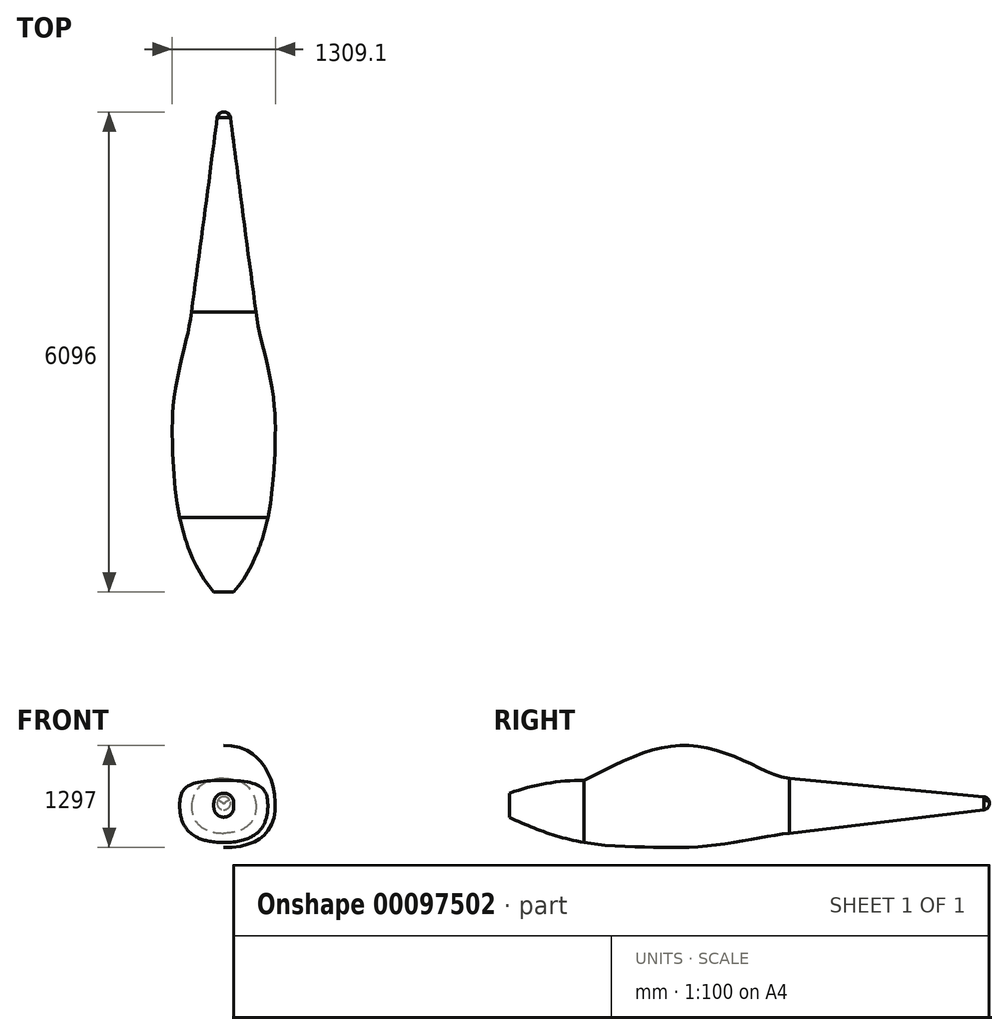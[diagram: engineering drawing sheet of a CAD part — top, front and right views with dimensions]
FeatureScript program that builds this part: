
annotation { "Feature Type Name" : "Feature", "Feature Type Description" : "" }
export const myFeature = defineFeature(function(context is Context, id is Id, definition is map)
    precondition{}
    {
        {
            var Q0;
            Q0=qCreatedBy(makeId("Right.planeOp"),FACE);
            var sketch = newSketch(context, id + "F0", { "sketchPlane" : qUnion([Q0])});
            skPoint(sketch, "E0", {"position": v(6096, 0) * mm});
            skLineSegment(sketch, "E1", {"start": v(0, 127) * mm, "end": v(0, -177.8) * mm, "construction": true});
            skLineSegment(sketch, "E2", {"start": v(3556, 317.5) * mm, "end": v(6096, 76.2) * mm});
            skLineSegment(sketch, "E3", {"start": v(3556, -381) * mm, "end": v(6096, -76.2) * mm});
            skLineSegment(sketch, "E4", {"start": v(6096, 76.2) * mm, "end": v(6096, -76.2) * mm});
            skFitSpline(sketch, "E5", {"points": [v(3556, 317.5) * mm, v(3071.36, 497.5) * mm, v(2421.88, 718.32) * mm, v(1768.58, 660.46) * mm, v(947.27, 290.82) * mm], "startDerivative": vector(-2336.2, 221.94) * mm, "endDerivative": vector(-2919.53, -1478.23) * mm});
            skArc(sketch, "E6", {"start": v(947.27, 290.82) * mm, "mid": v(466.6, 249.56) * mm, "end": v(0, 127) * mm});
            skLineSegment(sketch, "E7", {"start": v(947.27, 290.82) * mm, "end": v(1552.32, 290.82) * mm, "construction": true});
            skLineSegment(sketch, "E8", {"start": v(3556, 317.5) * mm, "end": v(3556, -381) * mm, "construction": true});
            skLineSegment(sketch, "E9", {"start": v(0, 0) * mm, "end": v(6096, 0) * mm, "construction": true});
            skFitSpline(sketch, "E10", {"points": [v(0, -177.8) * mm, v(947.27, -499.76) * mm, v(1768.58, -558.74) * mm, v(2421.88, -551.68) * mm, v(3071.36, -461.35) * mm, v(3556, -381) * mm], "startDerivative": vector(4121.91, -2025.5) * mm, "endDerivative": vector(3446.33, 413.56) * mm});
            skLineSegment(sketch, "E11", {"start": v(947.27, 290.82) * mm, "end": v(947.27, -499.76) * mm, "construction": true});
            skSolve(sketch);
        }
        {
            var Q0;
            Q0=qCreatedBy(makeId("Top.planeOp"),FACE);
            var sketch = newSketch(context, id + "F1", { "sketchPlane" : qUnion([Q0])});
            skPoint(sketch, "E12", {"position": v(0, 0) * mm});
            skPoint(sketch, "E13", {"position": v(0, 4938.15) * mm});
            skLineSegment(sketch, "E14", {"start": v(0, -719) * mm, "end": v(0, 5523.82) * mm, "construction": true});
            skLineSegment(sketch, "E15", {"start": v(-6987.12, -719) * mm, "end": v(5143.5, 8679) * mm, "construction": true});
            skLineSegment(sketch, "E16", {"start": v(0, 0) * mm, "end": v(127, 0) * mm, "construction": true});
            skPoint(sketch, "E17", {"position": v(0, 3556) * mm});
            skLineSegment(sketch, "E18", {"start": v(0, 3556) * mm, "end": v(406.4, 3556) * mm, "construction": true});
            skLineSegment(sketch, "E19", {"start": v(0, 6096) * mm, "end": v(76.2, 6096) * mm, "construction": true});
            skLineSegment(sketch, "E20", {"start": v(76.2, 6096) * mm, "end": v(406.4, 3556) * mm});
            skFitSpline(sketch, "E21", {"points": [v(406.4, 3556) * mm, v(508, 3071.36) * mm, v(635, 2421.88) * mm, v(647.7, 1768.58) * mm, v(558.8, 947.27) * mm, v(127, 0) * mm], "startDerivative": vector(419.27, -3225.13) * mm, "endDerivative": vector(-3018.7, -3495.33) * mm, "construction": true});
            skFitSpline(sketch, "E22", {"points": [v(558.8, 947.27) * mm, v(647.7, 1768.58) * mm, v(635, 2421.88) * mm, v(508, 3071.36) * mm, v(406.4, 3556) * mm], "startDerivative": vector(669, 3233.18) * mm, "endDerivative": vector(-318.72, 2451.72) * mm});
            skSolve(sketch);
        }
        {
            var Q0;
            Q0=qCreatedBy(makeId("Front.planeOp"),FACE);
            var sketch = newSketch(context, id + "F2", { "sketchPlane" : qUnion([Q0])});
            skArc(sketch, "E23", {"start": v(127, 0) * mm, "mid": v(89.8, 89.8) * mm, "end": v(0, 127) * mm});
            skArc(sketch, "E24", {"start": v(0, -177.8) * mm, "mid": v(89.8, -140.6) * mm, "end": v(127, -50.8) * mm});
            skLineSegment(sketch, "E25", {"start": v(127, 0) * mm, "end": v(127, -50.8) * mm});
            skLineSegment(sketch, "E26", {"start": v(0, 127) * mm, "end": v(0, -177.8) * mm});
            skLineSegment(sketch, "E27", {"start": v(0, -177.8) * mm, "end": v(-68.56, -177.8) * mm, "construction": true});
            skSolve(sketch);
        }
        {
            var Q0;
            Q0=sQuery(id+"F0.wireOp",VERTEX,"E6.start");
            var Q1;
            Q1=sQuery(id+"F1.wireOp",VERTEX,"E21.4.internal");
            var Q2;
            Q2=sQuery(id+"F0.wireOp",VERTEX,"E10.1.internal");
            cPlane(context, id + "F3", {"entities" : qUnion([Q0, Q1, Q2]), "cplaneType" : CPlaneType.THREE_POINT, "offset" : 152.4 * mm, "width" : 152.4 * mm, "height" : 152.4 * mm});
        }
        {
            var Q0;
            Q0=qCreatedBy(id+"F3.planeOp",FACE);
            var sketch = newSketch(context, id + "F4", { "sketchPlane" : qUnion([Q0])});
            skLineSegment(sketch, "E28", {"start": v(0, 290.82) * mm, "end": v(-303.5, 290.82) * mm, "construction": true});
            skLineSegment(sketch, "E29", {"start": v(0, -499.76) * mm, "end": v(-303.5, -499.76) * mm, "construction": true});
            skLineSegment(sketch, "E30", {"start": v(0, 290.82) * mm, "end": v(0, -499.76) * mm});
            skFitSpline(sketch, "E31", {"points": [v(0, 290.82) * mm, v(558.8, 0) * mm, v(0, -499.76) * mm], "startDerivative": vector(3027.2, 0) * mm, "endDerivative": vector(-2921, 0) * mm});
            skSolve(sketch);
        }
        {
            var Q0;
            Q0=sQuery(id+"F0.wireOp",VERTEX,"E5.3.internal");
            var Q1;
            Q1=sQuery(id+"F1.wireOp",VERTEX,"E21.3.internal");
            var Q2;
            Q2=sQuery(id+"F0.wireOp",VERTEX,"E10.2.internal");
            cPlane(context, id + "F5", {"entities" : qUnion([Q0, Q1, Q2]), "cplaneType" : CPlaneType.THREE_POINT, "offset" : 152.4 * mm, "width" : 152.4 * mm, "height" : 152.4 * mm});
        }
        {
            var Q0;
            Q0=qCreatedBy(id+"F5.planeOp",FACE);
            var sketch = newSketch(context, id + "F6", { "sketchPlane" : qUnion([Q0])});
            skLineSegment(sketch, "E32", {"start": v(0, 660.46) * mm, "end": v(0, -558.74) * mm});
            skLineSegment(sketch, "E33", {"start": v(0, -558.74) * mm, "end": v(-265.3, -558.74) * mm, "construction": true});
            skLineSegment(sketch, "E34", {"start": v(0, 660.46) * mm, "end": v(-265.3, 660.46) * mm, "construction": true});
            skFitSpline(sketch, "E35", {"points": [v(0, 660.46) * mm, v(647.7, 0) * mm, v(0, -558.74) * mm], "startDerivative": vector(2690.55, 0) * mm, "endDerivative": vector(-3108.83, 0) * mm});
            skSolve(sketch);
        }
        {
            var Q0;
            Q0=sQuery(id+"F0.wireOp",VERTEX,"E5.2.internal");
            var Q1;
            Q1=sQuery(id+"F1.wireOp",VERTEX,"E21.2.internal");
            var Q2;
            Q2=sQuery(id+"F0.wireOp",VERTEX,"E10.3.internal");
            cPlane(context, id + "F7", {"entities" : qUnion([Q0, Q1, Q2]), "cplaneType" : CPlaneType.THREE_POINT, "offset" : 152.4 * mm, "width" : 152.4 * mm, "height" : 152.4 * mm});
        }
        {
            var Q0;
            Q0=qCreatedBy(id+"F7.planeOp",FACE);
            var sketch = newSketch(context, id + "F8", { "sketchPlane" : qUnion([Q0])});
            skLineSegment(sketch, "E36", {"start": v(-313.1, 718.32) * mm, "end": v(0, 718.32) * mm, "construction": true});
            skLineSegment(sketch, "E37", {"start": v(0, 718.32) * mm, "end": v(0, -551.68) * mm});
            skLineSegment(sketch, "E38", {"start": v(0, -551.68) * mm, "end": v(-313.1, -551.68) * mm, "construction": true});
            skFitSpline(sketch, "E39", {"points": [v(0, 718.32) * mm, v(635, 0) * mm, v(0, -551.68) * mm], "startDerivative": vector(2656.34, 0) * mm, "endDerivative": vector(-3151.03, 0) * mm});
            skSolve(sketch);
        }
        {
            var Q0;
            Q0=sQuery(id+"F0.wireOp",VERTEX,"E5.1.internal");
            var Q1;
            Q1=sQuery(id+"F1.wireOp",VERTEX,"E21.1.internal");
            var Q2;
            Q2=sQuery(id+"F0.wireOp",VERTEX,"E10.4.internal");
            cPlane(context, id + "F9", {"entities" : qUnion([Q0, Q1, Q2]), "cplaneType" : CPlaneType.THREE_POINT, "offset" : 152.4 * mm, "width" : 152.4 * mm, "height" : 152.4 * mm});
        }
        {
            var Q0;
            Q0=qCreatedBy(id+"F9.planeOp",FACE);
            var sketch = newSketch(context, id + "F10", { "sketchPlane" : qUnion([Q0])});
            skLineSegment(sketch, "E40", {"start": v(-243.65, 497.5) * mm, "end": v(0, 497.5) * mm, "construction": true});
            skLineSegment(sketch, "E41", {"start": v(0, 497.5) * mm, "end": v(0, -461.35) * mm});
            skLineSegment(sketch, "E42", {"start": v(0, -461.35) * mm, "end": v(-243.65, -461.35) * mm, "construction": true});
            skFitSpline(sketch, "E43", {"points": [v(0, 497.5) * mm, v(508, 0) * mm, v(0, -461.35) * mm], "startDerivative": vector(2265.88, 0) * mm, "endDerivative": vector(-2614.01, 0) * mm});
            skSolve(sketch);
        }
        {
            var Q0;
            Q0=sQuery(id+"F0.wireOp",VERTEX,"E2.start");
            var Q1;
            Q1=sQuery(id+"F1.wireOp",VERTEX,"E20.end");
            var Q2;
            Q2=sQuery(id+"F0.wireOp",VERTEX,"E8.end");
            cPlane(context, id + "F11", {"entities" : qUnion([Q0, Q1, Q2]), "cplaneType" : CPlaneType.THREE_POINT, "offset" : 152.4 * mm, "width" : 152.4 * mm, "height" : 152.4 * mm});
        }
        {
            var Q0;
            Q0=qCreatedBy(id+"F11.planeOp",FACE);
            var sketch = newSketch(context, id + "F12", { "sketchPlane" : qUnion([Q0])});
            skLineSegment(sketch, "E44", {"start": v(-254, 317.5) * mm, "end": v(0, 317.5) * mm, "construction": true});
            skLineSegment(sketch, "E45", {"start": v(0, 317.5) * mm, "end": v(0, -381) * mm});
            skLineSegment(sketch, "E46", {"start": v(0, -381) * mm, "end": v(-254, -381) * mm, "construction": true});
            skFitSpline(sketch, "E47", {"points": [v(0, 317.5) * mm, v(406.4, 0) * mm, v(0, -381) * mm], "startDerivative": vector(1553.96, 0) * mm, "endDerivative": vector(-1943.73, 0) * mm});
            skSolve(sketch);
        }
        {
            var Q0;
            Q0=sQuery(id+"F0.wireOp",VERTEX,"E2.end");
            var Q1;
            Q1=sQuery(id+"F1.wireOp",VERTEX,"E19.end");
            var Q2;
            Q2=sQuery(id+"F0.wireOp",VERTEX,"E4.end");
            cPlane(context, id + "F13", {"entities" : qUnion([Q0, Q1, Q2]), "cplaneType" : CPlaneType.THREE_POINT, "offset" : 152.4 * mm, "width" : 152.4 * mm, "height" : 152.4 * mm});
        }
        {
            var Q0;
            Q0=qCreatedBy(id+"F13.planeOp",FACE);
            var sketch = newSketch(context, id + "F14", { "sketchPlane" : qUnion([Q0])});
            skArc(sketch, "E48", {"start": v(0, -76.2) * mm, "mid": v(76.2, 0) * mm, "end": v(0, 76.2) * mm});
            skLineSegment(sketch, "E49", {"start": v(0, 76.2) * mm, "end": v(0, -76.2) * mm});
            skSolve(sketch);
        }
        {
            var Q0;
            Q0=qCreatedBy(makeId("Right.planeOp"),FACE);
            var sketch = newSketch(context, id + "F15", { "sketchPlane" : qUnion([Q0])});
            skFitSpline(sketch, "E50", {"points": [v(0, -177.8) * mm, v(947.27, -499.76) * mm], "startDerivative": vector(903.58, -444.02) * mm, "endDerivative": vector(1097.35, -206.55) * mm});
            skSolve(sketch);
        }
        {
            var Q0;
            Q0=qCreatedBy(makeId("Top.planeOp"),FACE);
            var sketch = newSketch(context, id + "F16", { "sketchPlane" : qUnion([Q0])});
            skFitSpline(sketch, "E51", {"points": [v(127, 0) * mm, v(438.27, 531.01) * mm, v(558.8, 947.27) * mm], "startDerivative": vector(781.47, 904.86) * mm, "endDerivative": vector(204.1, 910.7) * mm});
            skSolve(sketch);
        }
        {
            var Q0;
            Q0=makeQuery(id+"F2.imprint","IMPRINT",FACE,{"disambiguationData":[TD([[makeQuery(id+"F2.imprint","IMPRINT",EDGE,{"derivedFrom":sQuery(id+"F2.wireOp",EDGE,"E23")}),1.0]])]});
            var Q1;
            Q1=makeQuery(id+"F4.imprint","IMPRINT",FACE,{"disambiguationData":[TD([[makeQuery(id+"F4.imprint","IMPRINT",EDGE,{"derivedFrom":sQuery(id+"F4.wireOp",EDGE,"E30")}),1.0]])]});
            var Q2;
            Q2=sQuery(id+"F0.wireOp",EDGE,"E6");
            var Q3;
            Q3=sQuery(id+"F15.wireOp",EDGE,"E50");
            var Q4;
            Q4=sQuery(id+"F16.wireOp",EDGE,"E51");
            loft(context, id + "F17", {"addGuides" : true, "sheetProfilesArray" : [{ "sheetProfileEntities" : qUnion([Q0]) }, { "sheetProfileEntities" : qUnion([Q1]) }], "guidesArray" : [{ "guideEntities" : qUnion([Q2]), "guideDerivativeType" : LoftGuideDerivativeType.DEFAULT, "guideDerivativeMagnitude" : 1 }, { "guideEntities" : qUnion([Q3]), "guideDerivativeType" : LoftGuideDerivativeType.DEFAULT, "guideDerivativeMagnitude" : 1 }, { "guideEntities" : qUnion([Q4]), "guideDerivativeType" : LoftGuideDerivativeType.DEFAULT, "guideDerivativeMagnitude" : 1 }]});
        }
        {
            var Q0;
            Q0=qCreatedBy(makeId("Right.planeOp"),FACE);
            var sketch = newSketch(context, id + "F18", { "sketchPlane" : qUnion([Q0])});
            skFitSpline(sketch, "E52", {"points": [v(947.27, -499.76) * mm, v(1768.58, -558.74) * mm, v(2421.88, -551.68) * mm, v(3071.36, -461.35) * mm, v(3556, -381) * mm], "startDerivative": vector(3130, -509) * mm, "endDerivative": vector(2033.65, 244.04) * mm});
            skSolve(sketch);
        }
        {
            var Q1;
            Q1=makeQuery(id+"F17.opLoft","CAP_FACE",FACE,{"disambiguationData":[OSD([makeQuery(id+"F4.imprint","IMPRINT",FACE,{"disambiguationData":[TD([[makeQuery(id+"F4.imprint","IMPRINT",EDGE,{"derivedFrom":sQuery(id+"F4.wireOp",EDGE,"E30")}),1.0]])]})])],"isStart":true});
            var Q2;
            Q2=makeQuery(id+"F6.imprint","IMPRINT",FACE,{"disambiguationData":[TD([[makeQuery(id+"F6.imprint","IMPRINT",EDGE,{"derivedFrom":sQuery(id+"F6.wireOp",EDGE,"E32")}),1.0]])]});
            var Q3;
            Q3=makeQuery(id+"F8.imprint","IMPRINT",FACE,{"disambiguationData":[TD([[makeQuery(id+"F8.imprint","IMPRINT",EDGE,{"derivedFrom":sQuery(id+"F8.wireOp",EDGE,"E37")}),1.0]])]});
            var Q4;
            Q4=makeQuery(id+"F10.imprint","IMPRINT",FACE,{"disambiguationData":[TD([[makeQuery(id+"F10.imprint","IMPRINT",EDGE,{"derivedFrom":sQuery(id+"F10.wireOp",EDGE,"E41")}),1.0]])]});
            var Q5;
            Q5=makeQuery(id+"F12.imprint","IMPRINT",FACE,{"disambiguationData":[TD([[makeQuery(id+"F12.imprint","IMPRINT",EDGE,{"derivedFrom":sQuery(id+"F12.wireOp",EDGE,"E45")}),1.0]])]});
            var Q6;
            Q6=sQuery(id+"F1.wireOp",EDGE,"E22");
            var Q7;
            Q7=sQuery(id+"F0.wireOp",EDGE,"E5");
            var Q8;
            Q8=sQuery(id+"F18.wireOp",EDGE,"E52");
            loft(context, id + "F19", {"operationType" : NewBodyOperationType.ADD, "addGuides" : true, "sheetProfilesArray" : [{ "sheetProfileEntities" : qUnion([Q1]) }, { "sheetProfileEntities" : qUnion([Q2]) }, { "sheetProfileEntities" : qUnion([Q3]) }, { "sheetProfileEntities" : qUnion([Q4]) }, { "sheetProfileEntities" : qUnion([Q5]) }], "guidesArray" : [{ "guideEntities" : qUnion([Q6]), "guideDerivativeType" : LoftGuideDerivativeType.DEFAULT, "guideDerivativeMagnitude" : 1 }, { "guideEntities" : qUnion([Q7]), "guideDerivativeType" : LoftGuideDerivativeType.DEFAULT, "guideDerivativeMagnitude" : 1 }, { "guideEntities" : qUnion([Q8]), "guideDerivativeType" : LoftGuideDerivativeType.DEFAULT, "guideDerivativeMagnitude" : 1 }]});
        }
        {
            var Q1;
            Q1=makeQuery(id+"F19.opLoft","CAP_FACE",FACE,{"disambiguationData":[OSD([makeQuery(id+"F12.imprint","IMPRINT",FACE,{"disambiguationData":[TD([[makeQuery(id+"F12.imprint","IMPRINT",EDGE,{"derivedFrom":sQuery(id+"F12.wireOp",EDGE,"E45")}),1.0]])]})])],"isStart":true});
            var Q2;
            Q2=makeQuery(id+"F14.imprint","IMPRINT",FACE,{"disambiguationData":[TD([[makeQuery(id+"F14.imprint","IMPRINT",EDGE,{"derivedFrom":sQuery(id+"F14.wireOp",EDGE,"E48")}),1.0]])]});
            var Q3;
            Q3=sQuery(id+"F0.wireOp",EDGE,"E2");
            var Q4;
            Q4=sQuery(id+"F0.wireOp",EDGE,"E3");
            loft(context, id + "F20", {"operationType" : NewBodyOperationType.ADD, "addGuides" : true, "sheetProfilesArray" : [{ "sheetProfileEntities" : qUnion([Q1]) }, { "sheetProfileEntities" : qUnion([Q2]) }], "guidesArray" : [{ "guideEntities" : qUnion([Q3]), "guideDerivativeType" : LoftGuideDerivativeType.DEFAULT, "guideDerivativeMagnitude" : 1 }, { "guideEntities" : qUnion([Q4]), "guideDerivativeType" : LoftGuideDerivativeType.DEFAULT, "guideDerivativeMagnitude" : 1 }]});
        }
        {
            var Q0;
            Q0=makeQuery(id+"F17.opLoft","SWEPT_BODY",BODY,{"disambiguationData":[OSD([sQuery(id+"F0.wireOp",EDGE,"E6"),makeQuery(id+"F2.imprint","IMPRINT",FACE,{"disambiguationData":[TD([[makeQuery(id+"F2.imprint","IMPRINT",EDGE,{"derivedFrom":sQuery(id+"F2.wireOp",EDGE,"E23")}),1.0]])]}),makeQuery(id+"F4.imprint","IMPRINT",FACE,{"disambiguationData":[TD([[makeQuery(id+"F4.imprint","IMPRINT",EDGE,{"derivedFrom":sQuery(id+"F4.wireOp",EDGE,"E30")}),1.0]])]}),sQuery(id+"F15.wireOp",EDGE,"E50"),sQuery(id+"F16.wireOp",EDGE,"E51")])]});
            var Q1;
            Q1=qCreatedBy(makeId("Right.planeOp"),FACE);
            mirror(context, id + "F21", {"operationType" : NewBodyOperationType.ADD, "entities" : qUnion([Q0]), "mirrorPlane" : qUnion([Q1])});
        }
        {
            var Q0;
            Q0=makeQuery(id+"F20.opLoft","MID_CAP_EDGE",EDGE,{"disambiguationData":[OSD([sQuery(id+"F0.wireOp",EDGE,"E2"),sQuery(id+"F14.wireOp",EDGE,"E48")])],"capPos":1.0});
            var Q1;
            Q1=makeQuery(id+"F20.opLoft","MID_CAP_EDGE",EDGE,{"disambiguationData":[OSD([sQuery(id+"F0.wireOp",EDGE,"E2"),sQuery(id+"F1.wireOp",EDGE,"E22"),sQuery(id+"F14.wireOp",EDGE,"E48")])],"capPos":1.0});
            var Q2;
            Q2=makeQuery(id+"F20.opLoft","MID_CAP_EDGE",EDGE,{"disambiguationData":[OSD([sQuery(id+"F0.wireOp",EDGE,"E3"),sQuery(id+"F1.wireOp",EDGE,"E22"),sQuery(id+"F14.wireOp",EDGE,"E48")])],"capPos":1.0});
            var Q3;
            Q3=makeQuery(id+"F21.opPattern","COPY",EDGE,{"derivedFrom":makeQuery(id+"F20.opLoft","MID_CAP_EDGE",EDGE,{"disambiguationData":[OSD([sQuery(id+"F0.wireOp",EDGE,"E3"),sQuery(id+"F1.wireOp",EDGE,"E22"),sQuery(id+"F14.wireOp",EDGE,"E48")])],"capPos":1.0}),"instanceName":"1"});
            var Q4;
            Q4=makeQuery(id+"F21.opPattern","COPY",EDGE,{"derivedFrom":makeQuery(id+"F20.opLoft","MID_CAP_EDGE",EDGE,{"disambiguationData":[OSD([sQuery(id+"F0.wireOp",EDGE,"E2"),sQuery(id+"F1.wireOp",EDGE,"E22"),sQuery(id+"F14.wireOp",EDGE,"E48")])],"capPos":1.0}),"instanceName":"1"});
            var Q5;
            Q5=makeQuery(id+"F21.opPattern","COPY",EDGE,{"derivedFrom":makeQuery(id+"F20.opLoft","MID_CAP_EDGE",EDGE,{"disambiguationData":[OSD([sQuery(id+"F0.wireOp",EDGE,"E2"),sQuery(id+"F14.wireOp",EDGE,"E48")])],"capPos":1.0}),"instanceName":"1"});
            fillet(context, id + "F22", {"entities" : qUnion([Q0, Q1, Q2, Q3, Q4, Q5]), "radius" : 76.2 * mm, "tangentPropagation" : true, "allowEdgeOverflow" : false});
        }
    });
